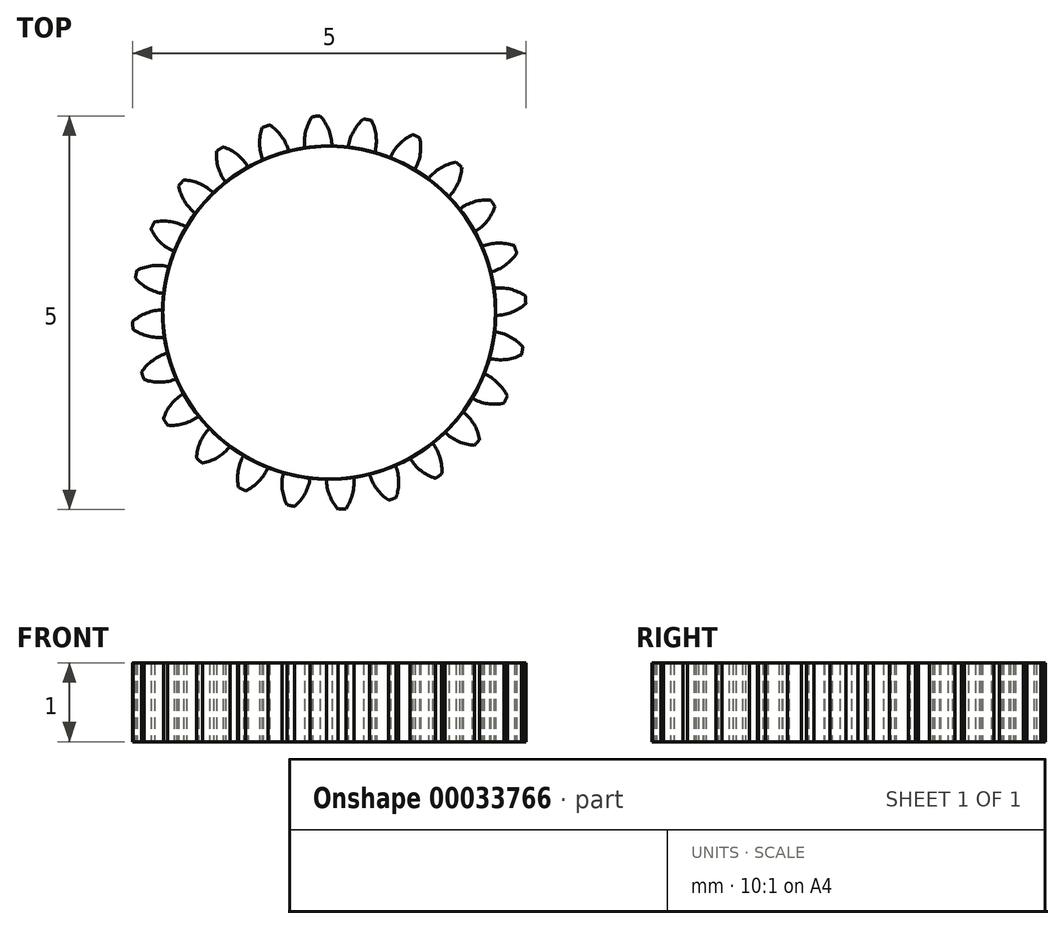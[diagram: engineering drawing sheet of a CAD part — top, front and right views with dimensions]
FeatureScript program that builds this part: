
annotation { "Feature Type Name" : "Feature", "Feature Type Description" : "" }
export const myFeature = defineFeature(function(context is Context, id is Id, definition is map)
    precondition{}
    {
        {
            assignVariable(context, id + "F0", {"name" : "N", "anyValue" : 24});
        }
        {
            var Q0;
            Q0=qCreatedBy(makeId("Top.planeOp"),FACE);
            var sketch = newSketch(context, id + "F1", { "sketchPlane" : qUnion([Q0])});
            skCircle(sketch, "E0", {"center": v(0, 0) * mm, "radius": 2.12 * mm});
            skCircle(sketch, "E1", {"center": v(0, 0) * mm, "radius": 2.3 * mm, "construction": true});
            skLineSegment(sketch, "E2", {"start": v(0, 0) * mm, "end": v(0, 2.5) * mm, "construction": true});
            skLineSegment(sketch, "E3", {"start": v(0, 0) * mm, "end": v(-0.16, 2.5) * mm, "construction": true});
            skLineSegment(sketch, "E4", {"start": v(0, 2.3) * mm, "end": v(-4.09, 2.3) * mm, "construction": true});
            skLineSegment(sketch, "E5", {"start": v(0, 2.3) * mm, "end": v(-4.07, 0.83) * mm, "construction": true});
            skCircle(sketch, "E6", {"center": v(0, 2.3) * mm, "radius": 0.58 * mm, "construction": true});
            skArc(sketch, "E7", {"start": v(-0.11, 2.5) * mm, "mid": v(-1.08, 1.9) * mm, "end": v(0.03, 2.12) * mm, "construction": true});
            skArc(sketch, "E8", {"start": v(0.03, 2.12) * mm, "mid": v(0, 2.32) * mm, "end": v(-0.11, 2.5) * mm});
            skArc(sketch, "E9.MirrorCS", {"start": v(-0.31, 2.1) * mm, "mid": v(-0.3, 2.3) * mm, "end": v(-0.21, 2.5) * mm});
            skArc(sketch, "E10", {"start": v(-0.21, 2.5) * mm, "mid": v(0.16, -2.5) * mm, "end": v(-0.11, 2.5) * mm, "construction": true});
            skArc(sketch, "E11", {"start": v(-0.11, 2.5) * mm, "mid": v(-0.16, 2.5) * mm, "end": v(-0.21, 2.5) * mm});
            skSolve(sketch);
        }
        {
            var Q0;
            {var subQ0=sQuery(id+"F1.wireOp",EDGE,"E0");var subQ2=makeQuery(id+"F1.imprint","INTERSECT",VERTEX,{"derivedFrom":[subQ0,sQuery(id+"F1.wireOp",EDGE,"E8")]});Q0=makeQuery(id+"F1.imprint","IMPRINT",FACE,{"disambiguationData":[TD([[makeQuery(id+"F1.imprint","IMPRINT",EDGE,{"disambiguationData":[TD([[subQ2,-1.0]])],"derivedFrom":subQ0}),1.0]])]});}
            var Q1;
            {var subQ1=sQuery(id+"F1.wireOp",EDGE,"E8");Q1=makeQuery(id+"F1.imprint","IMPRINT",FACE,{"disambiguationData":[TD([[makeQuery(id+"F1.imprint","IMPRINT",EDGE,{"derivedFrom":subQ1}),1.0]])]});}
            extrude(context, id + "F2", {"entities" : qUnion([Q0, Q1]), "depth" : 1 * mm});
        }
        {
            var Q0;
            Q0=makeQuery(id+"F2.opExtrude","SWEPT_BODY",BODY,{"disambiguationData":[OSD([sQuery(id+"F1.wireOp",EDGE,"E0"),sQuery(id+"F1.wireOp",EDGE,"E8"),sQuery(id+"F1.wireOp",EDGE,"E9.MirrorCS"),sQuery(id+"F1.wireOp",EDGE,"E11")])]});
            var Q1;
            Q1=makeQuery(id+"F2.opExtrude","CAP_EDGE",EDGE,{"disambiguationData":[OSD([sQuery(id+"F1.wireOp",EDGE,"E0")])],"isStart":false});
            circularPattern(context, id + "F3", {"entities" : qUnion([Q0]), "axis" : qUnion([Q1]), "angle" : (360 / getVariable(context, 'N')) * degree, "instanceCount" : getVariable(context, 'N')});
        }
    });
